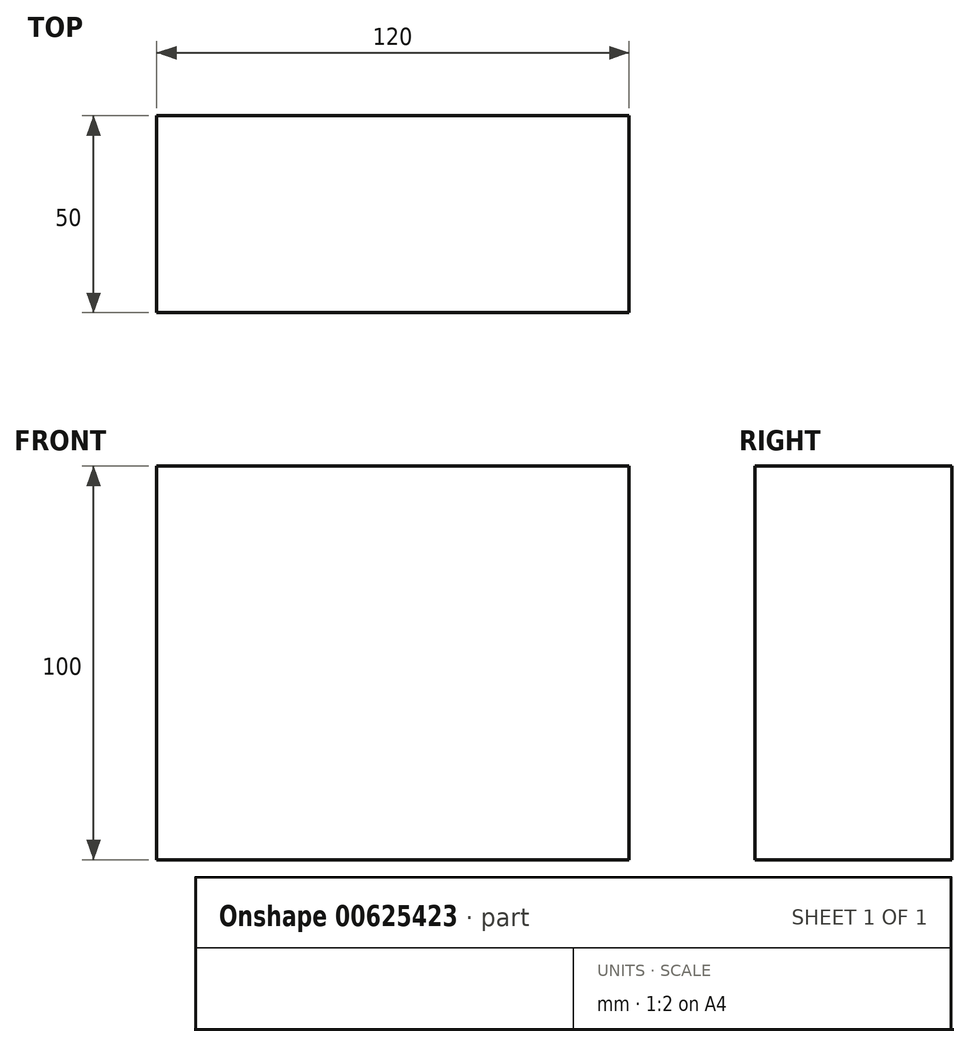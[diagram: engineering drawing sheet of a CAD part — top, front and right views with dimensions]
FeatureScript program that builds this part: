
annotation { "Feature Type Name" : "Feature", "Feature Type Description" : "" }
export const myFeature = defineFeature(function(context is Context, id is Id, definition is map)
    precondition{}
    {
        {
            var Q0;
            Q0=qCreatedBy(makeId("Front.planeOp"),FACE);
            var sketch = newSketch(context, id + "F0", { "sketchPlane" : qUnion([Q0])});
            skLineSegment(sketch, "E0.bottom", {"start": v(60, -50) * mm, "end": v(-60, -50) * mm});
            skLineSegment(sketch, "E0.top", {"start": v(60, 50) * mm, "end": v(-60, 50) * mm});
            skLineSegment(sketch, "E0.left", {"start": v(60, -50) * mm, "end": v(60, 50) * mm});
            skLineSegment(sketch, "E0.right", {"start": v(-60, -50) * mm, "end": v(-60, 50) * mm});
            skPoint(sketch, "E0.middle", {"position": v(0, 0) * mm});
            skSolve(sketch);
        }
        {
            var Q0;
            Q0=makeQuery(id+"F0.imprint","IMPRINT",FACE,{"disambiguationData":[TD([[makeQuery(id+"F0.imprint","IMPRINT",EDGE,{"derivedFrom":sQuery(id+"F0.wireOp",EDGE,"E0.bottom")}),-1.0]])]});
            extrude(context, id + "F1", {"entities" : qUnion([Q0]), "depth" : 50 * mm, "offsetDistance" : 25 * mm});
        }
    });
